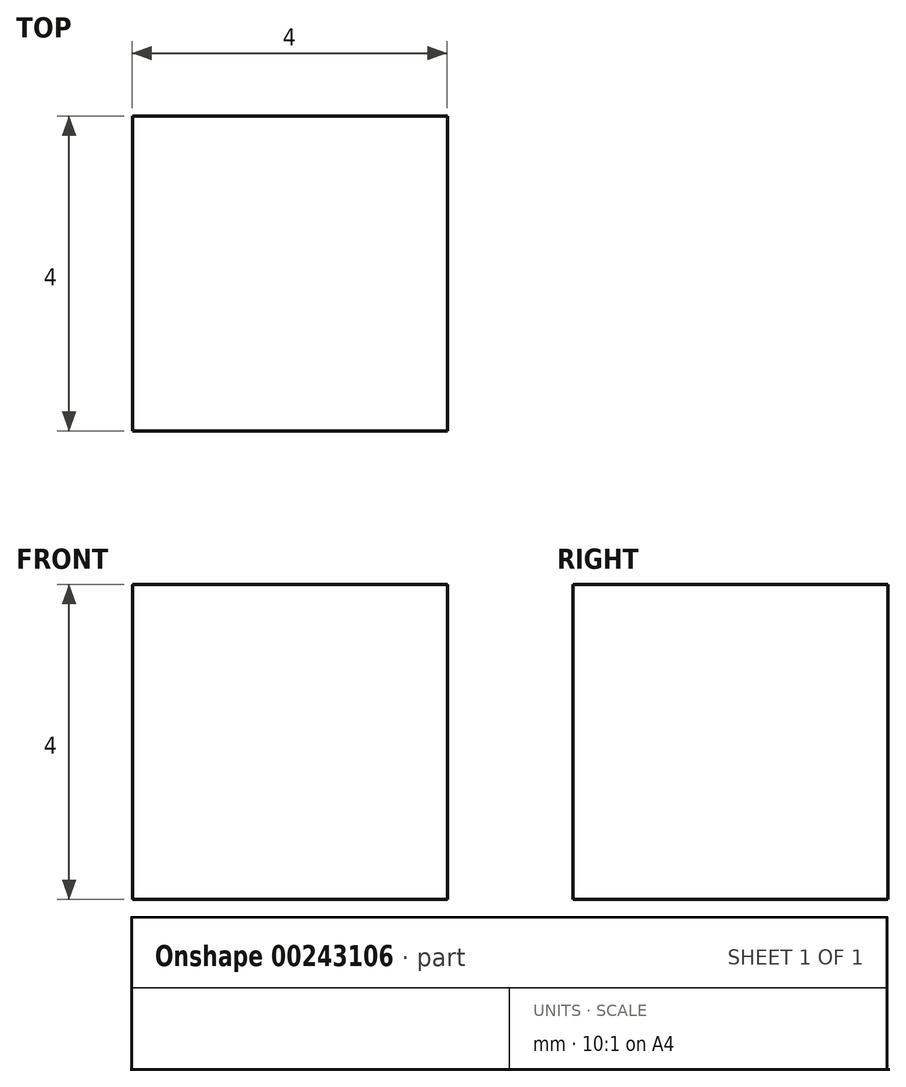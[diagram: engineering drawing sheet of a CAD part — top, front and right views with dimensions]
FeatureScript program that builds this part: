
annotation { "Feature Type Name" : "Feature", "Feature Type Description" : "" }
export const myFeature = defineFeature(function(context is Context, id is Id, definition is map)
    precondition{}
    {
        {
            var Q0;
            Q0=qCreatedBy(makeId("Top.planeOp"),FACE);
            var sketch = newSketch(context, id + "F0", { "sketchPlane" : qUnion([Q0])});
            skLineSegment(sketch, "E0.bottom", {"start": v(7.88, 10.31) * mm, "end": v(11.88, 10.31) * mm});
            skLineSegment(sketch, "E0.top", {"start": v(7.88, 6.31) * mm, "end": v(11.88, 6.31) * mm});
            skLineSegment(sketch, "E0.left", {"start": v(7.88, 10.31) * mm, "end": v(7.88, 6.31) * mm});
            skLineSegment(sketch, "E0.right", {"start": v(11.88, 10.31) * mm, "end": v(11.88, 6.31) * mm});
            skSolve(sketch);
        }
        {
            var Q0;
            Q0 = qSketchRegion(id + "F0", true);
            extrude(context, id + "F1", {"entities" : qUnion([Q0]), "depth" : 4 * mm});
        }
    });
